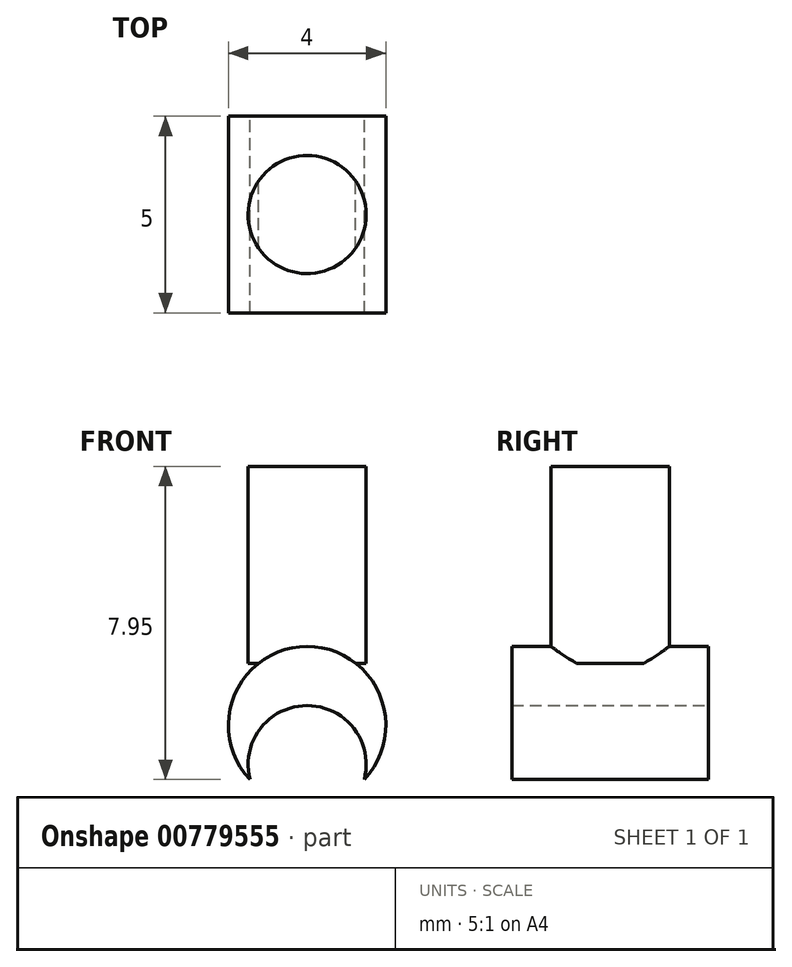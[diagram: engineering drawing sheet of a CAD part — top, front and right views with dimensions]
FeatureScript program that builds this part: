
annotation { "Feature Type Name" : "Feature", "Feature Type Description" : "" }
export const myFeature = defineFeature(function(context is Context, id is Id, definition is map)
    precondition{}
    {
        {
            var Q0;
            Q0=qCreatedBy(makeId("Front.planeOp"),FACE);
            var sketch = newSketch(context, id + "F0", { "sketchPlane" : qUnion([Q0])});
            skArc(sketch, "E0", {"start": v(1.45, -2.95) * mm, "mid": v(0, 0.43) * mm, "end": v(-1.45, -2.95) * mm});
            skArc(sketch, "E1", {"start": v(1.45, -2.95) * mm, "mid": v(0, -1.07) * mm, "end": v(-1.45, -2.95) * mm});
            skSolve(sketch);
        }
        {
            var Q0;
            Q0 = qSketchRegion(id + "F0", true);
            extrude(context, id + "F1", {"entities" : qUnion([Q0]), "endBound" : BoundingType.SYMMETRIC, "depth" : 5 * mm, "offsetDistance" : 25 * mm});
        }
        {
            var Q0;
            Q0=qCreatedBy(makeId("Top.planeOp"),FACE);
            var sketch = newSketch(context, id + "F2", { "sketchPlane" : qUnion([Q0])});
            skCircle(sketch, "E2", {"center": v(0, 0) * mm, "radius": 1.5 * mm});
            skSolve(sketch);
        }
        {
            var Q0;
            Q0 = qSketchRegion(id + "F2", true);
            extrude(context, id + "F3", {"entities" : qUnion([Q0]), "operationType" : NewBodyOperationType.ADD, "depth" : 5 * mm, "offsetDistance" : 25 * mm});
        }
    });
